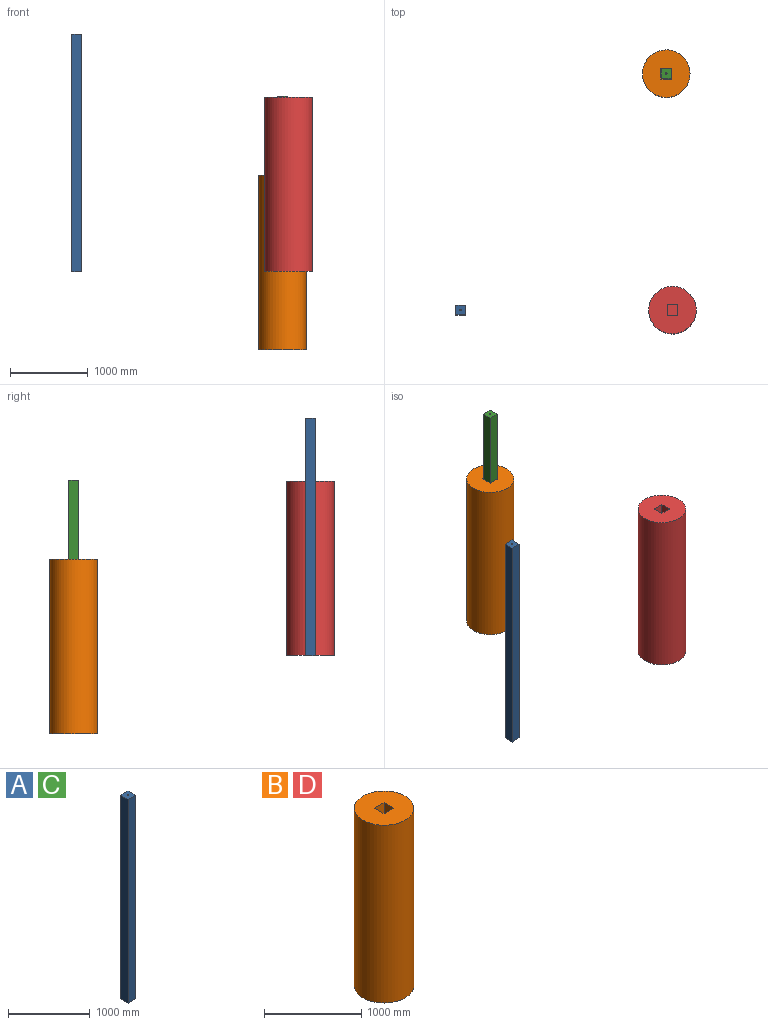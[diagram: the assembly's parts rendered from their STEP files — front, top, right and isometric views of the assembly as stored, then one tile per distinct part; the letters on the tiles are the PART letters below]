
ASSEMBLY  parts=4 mates=1
PART A: 8 faces, bbox 127x127x3048 mm
  f0: plane 3048x127mm, normal (-1,0,0), area 387096mm2, adj f1,f3,f4,f5
  f1: plane 3048x127mm, normal (0,-1,0), area 387096mm2, adj f0,f2,f4,f5
  f2: plane 3048x127mm, normal (1,0,0), area 387096mm2, adj f1,f3,f4,f5
  f3: plane 3048x127mm, normal (0,1,0), area 387096mm2, adj f0,f2,f4,f5
  f4: plane 127x127mm, normal (0,0,1), area 15844mm2, adj f0,f1,f2,f3,f6
  f5: plane 127x127mm, normal (0,0,-1), area 16129mm2, adj f0,f1,f2,f3
  f6: cylinder r=9.53mm len=127mm, axis (0,0,1), area 7600.6mm2, adj f4,f7
  f7: plane 19.05x19.05mm, normal (0,0,1), area 285mm2, adj f6
PART B: 8 faces, bbox 609.6x609.6x2235.2 mm
  f0: plane 2032x139.7mm, normal (0,1,0), area 283870.4mm2, adj f1,f3,f5,f7
  f1: plane 2032x139.7mm, normal (1,0,0), area 283870.4mm2, adj f0,f2,f5,f7
  f2: plane 2032x139.7mm, normal (0,-1,0), area 283870.4mm2, adj f1,f3,f5,f7
  f3: plane 2032x139.7mm, normal (-1,0,0), area 283870.4mm2, adj f0,f2,f5,f7
  f4: cylinder r=304.8mm len=2235.2mm, axis (0,0,-1), area 4280664.8mm2, adj f5,f6
  f5: plane 609.6x609.6mm, normal (0,0,1), area 272347.4mm2, adj f0,f1,f2,f3,f4
  f6: plane 609.6x609.6mm, normal (0,0,-1), area 291863.5mm2, adj f4
  f7: plane 139.7x139.7mm, normal (0,0,1), area 19516.1mm2, adj f0,f1,f2,f3
PART C: same geometry as A
PART D: same geometry as B
PLACE A t=(-1982.72,-1002.33,775.02)mm
PLACE B rot(axis=(-1,0,0),0deg) t=(706.07,2053.27,-222.28)mm
PLACE C rot(axis=(-1,0,0),0deg) t=(656.11,2033.73,-19.08)mm
PLACE D t=(785.04,-982.8,780.43)mm
MATE fastened C.f6 <-> B.f4  axis (0,0,-1) through (686.72,2039.83,-19.08)mm
